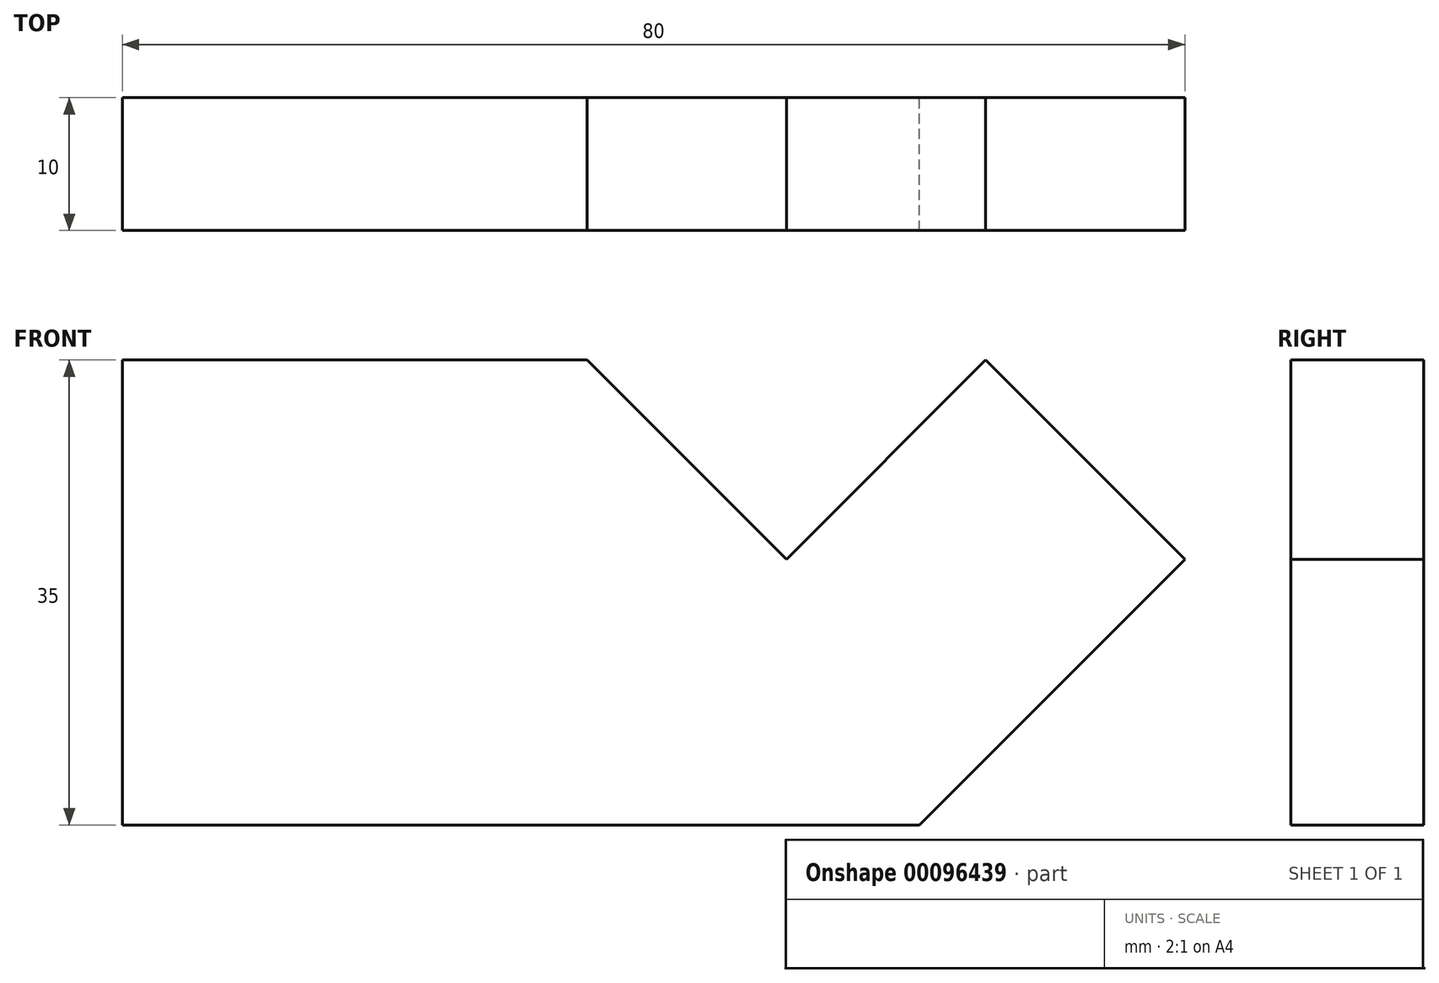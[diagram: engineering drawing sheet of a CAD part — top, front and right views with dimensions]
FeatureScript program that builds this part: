
annotation { "Feature Type Name" : "Feature", "Feature Type Description" : "" }
export const myFeature = defineFeature(function(context is Context, id is Id, definition is map)
    precondition{}
    {
        {
            var Q0;
            Q0=qCreatedBy(makeId("Front.planeOp"),FACE);
            var sketch = newSketch(context, id + "F0", { "sketchPlane" : qUnion([Q0])});
            skLineSegment(sketch, "E0", {"start": v(0, 0) * mm, "end": v(60, 0) * mm});
            skLineSegment(sketch, "E1", {"start": v(60, 0) * mm, "end": v(80, 20) * mm});
            skLineSegment(sketch, "E2", {"start": v(80, 20) * mm, "end": v(65, 35) * mm});
            skLineSegment(sketch, "E3", {"start": v(65, 35) * mm, "end": v(50, 20) * mm});
            skLineSegment(sketch, "E4", {"start": v(50, 20) * mm, "end": v(35, 35) * mm});
            skLineSegment(sketch, "E5", {"start": v(35, 35) * mm, "end": v(0, 35) * mm});
            skLineSegment(sketch, "E6", {"start": v(0, 35) * mm, "end": v(0, 0) * mm});
            skLineSegment(sketch, "E7", {"start": v(35, 35) * mm, "end": v(65, 35) * mm, "construction": true});
            skSolve(sketch);
        }
        {
            var Q0;
            Q0 = qSketchRegion(id + "F0", true);
            extrude(context, id + "F1", {"entities" : qUnion([Q0]), "depth" : 10 * mm});
        }
    });
